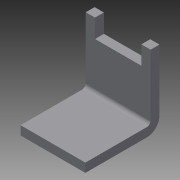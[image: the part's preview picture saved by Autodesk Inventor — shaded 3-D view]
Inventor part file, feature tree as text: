
AUTODESK INVENTOR PART (.ipt)
format: ipt  version: 2013 (Build 170138000, 138)  size: 122,368 bytes
history: native  units: in
note: dims shown in document units (in); Inventor stores cm internally (conversion verified against a paired STEP export)
features: sheet_metal_op x4, sketch x3, other x3
ambient origin geometry x8: Origin, YZ Plane, XZ Plane, XY Plane, X Axis, Y Axis, Z Axis, Center Point
bodies: Solid1 (feature_tree)
feature tree (10):
  sheet_metal_op  "Face1"
  sheet_metal_op  "Flange1"
  sketch  "Sketch1"  dims[d0=0.25in]
  other  "Plate1"
  sketch  "Sketch2"  dims[d1=0.125in]
  other  "Plate2"
  sheet_metal_op  "Bend1"
  sheet_metal_op  "Corner1"
  sketch  "Sketch3"  dims[d2=0.375in d3=0.625in d4=0.125in d6=0.625in d12=0.12in d13=0.12in d14=0.06in d15=0.24in d16=0.12in d17=1.0in d18=90.0deg d19=0.05in d20=0.48in d21=0.12in d22=0.12in d23=0.266in d24=0.266in d25=0.5in d26=0.5in d27=0.25in d28=0.25in d29=0.12in d30=0.0in]
  other  "Cut1"
